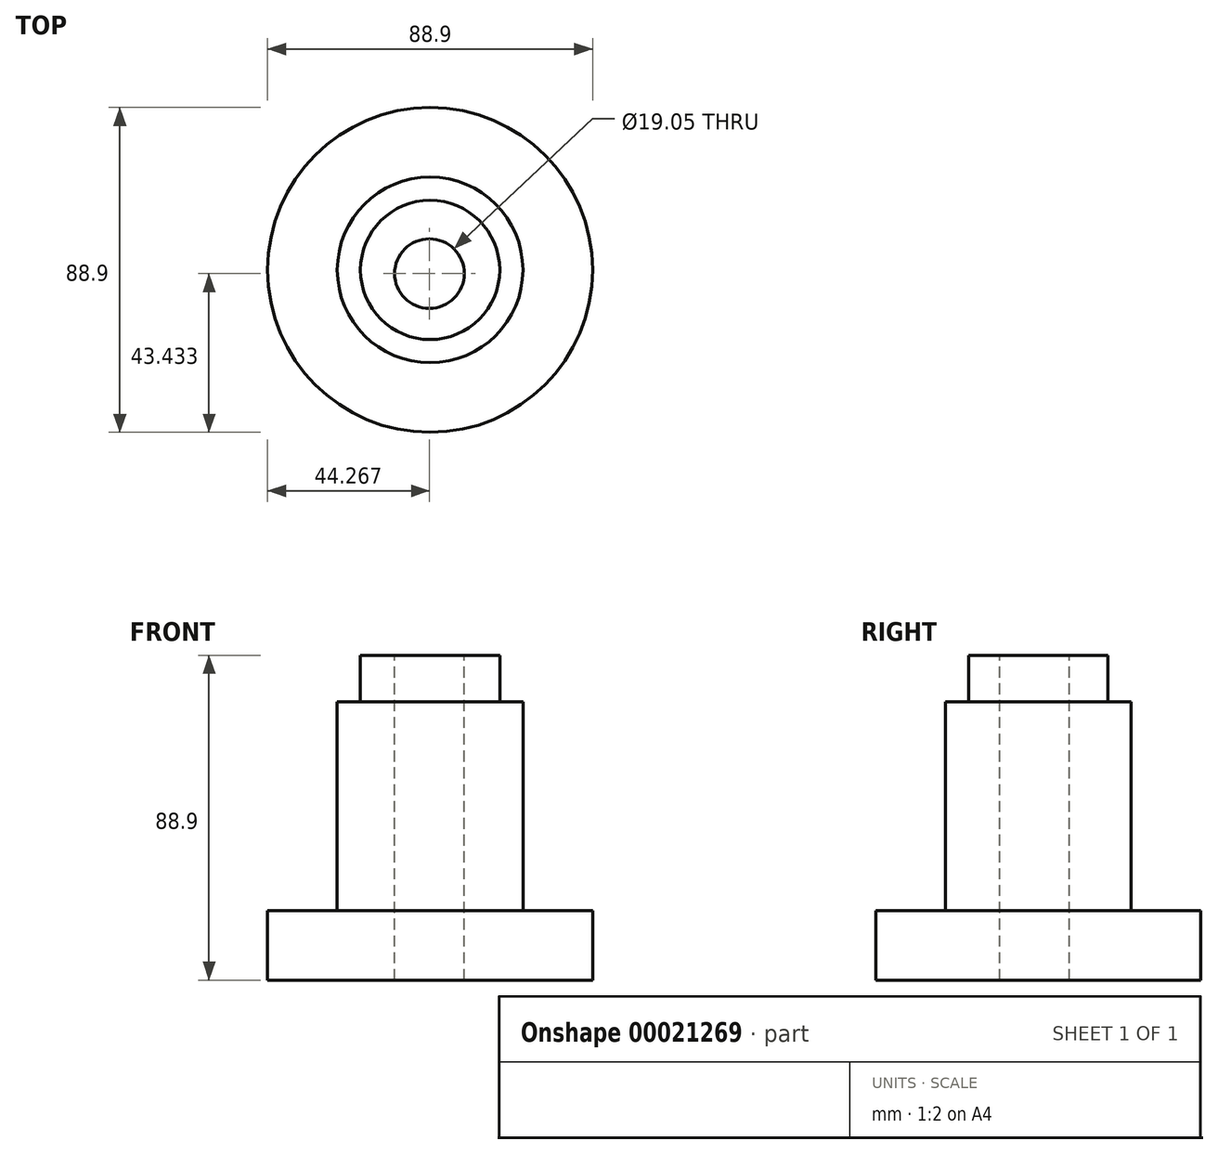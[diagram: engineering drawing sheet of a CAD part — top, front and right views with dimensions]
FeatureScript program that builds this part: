
annotation { "Feature Type Name" : "Feature", "Feature Type Description" : "" }
export const myFeature = defineFeature(function(context is Context, id is Id, definition is map)
    precondition{}
    {
        {
            var Q0;
            Q0=qCreatedBy(makeId("Front.planeOp"),FACE);
            var sketch = newSketch(context, id + "F0", { "sketchPlane" : qUnion([Q0])});
            skLineSegment(sketch, "E0.bottom", {"start": v(-65.1, -12.34) * mm, "end": v(-20.66, -12.34) * mm});
            skLineSegment(sketch, "E0.top", {"start": v(-65.1, -31.39) * mm, "end": v(-20.66, -31.39) * mm});
            skLineSegment(sketch, "E0.left", {"start": v(-65.1, -12.34) * mm, "end": v(-65.1, -31.39) * mm});
            skLineSegment(sketch, "E0.right", {"start": v(-20.66, -12.34) * mm, "end": v(-20.66, -31.39) * mm});
            skLineSegment(sketch, "E1.bottom", {"start": v(-46.06, 44.81) * mm, "end": v(-20.66, 44.81) * mm});
            skLineSegment(sketch, "E1.top", {"start": v(-46.06, -12.34) * mm, "end": v(-20.66, -12.34) * mm});
            skLineSegment(sketch, "E1.left", {"start": v(-46.06, 44.81) * mm, "end": v(-46.06, -12.34) * mm});
            skLineSegment(sketch, "E1.right", {"start": v(-20.66, 44.81) * mm, "end": v(-20.66, -12.34) * mm});
            skLineSegment(sketch, "E2.bottom", {"start": v(-39.7, 57.51) * mm, "end": v(-20.66, 57.51) * mm});
            skLineSegment(sketch, "E2.top", {"start": v(-39.7, 44.81) * mm, "end": v(-20.66, 44.81) * mm});
            skLineSegment(sketch, "E2.left", {"start": v(-39.7, 57.51) * mm, "end": v(-39.7, 44.81) * mm});
            skLineSegment(sketch, "E2.right", {"start": v(-20.66, 57.51) * mm, "end": v(-20.66, 44.81) * mm});
            skSolve(sketch);
        }
        {
            var Q0;
            Q0=makeQuery(id+"F0.imprint","IMPRINT",FACE,{"disambiguationData":[TD([[makeQuery(id+"F0.imprint","IMPRINT",EDGE,{"derivedFrom":sQuery(id+"F0.wireOp",EDGE,"E1.bottom")}),-1.0]])]});
            var Q1;
            Q1=makeQuery(id+"F0.imprint","IMPRINT",FACE,{"disambiguationData":[TD([[makeQuery(id+"F0.imprint","IMPRINT",EDGE,{"derivedFrom":sQuery(id+"F0.wireOp",EDGE,"E2.bottom")}),-1.0]])]});
            var Q2;
            Q2=makeQuery(id+"F0.imprint","IMPRINT",FACE,{"disambiguationData":[TD([[makeQuery(id+"F0.imprint","IMPRINT",EDGE,{"derivedFrom":sQuery(id+"F0.wireOp",EDGE,"E0.bottom")}),-1.0]])]});
            var Q3;
            Q3=sQuery(id+"F0.wireOp",EDGE,"E0.right");
            revolve(context, id + "F1", {"entities" : qUnion([Q0, Q1, Q2]), "axis" : qUnion([Q3]), "revolveType" : RevolveType.FULL});
        }
        {
            var Q0;
            Q0=qCreatedBy(makeId("Top.planeOp"),FACE);
            var sketch = newSketch(context, id + "F2", { "sketchPlane" : qUnion([Q0])});
            skCircle(sketch, "E3", {"center": v(-20.84, -1.02) * mm, "radius": 9.53 * mm});
            skSolve(sketch);
        }
        {
            var Q0;
            Q0 = qSketchRegion(id + "F2", true);
            extrude(context, id + "F3", {"entities" : qUnion([Q0]), "operationType" : NewBodyOperationType.REMOVE, "endBound" : BoundingType.THROUGH_ALL, "oppositeDirection" : true, "depth" : 25.4 * mm});
        }
        {
            var Q0;
            Q0 = qSketchRegion(id + "F2", true);
            extrude(context, id + "F4", {"entities" : qUnion([Q0]), "operationType" : NewBodyOperationType.REMOVE, "endBound" : BoundingType.THROUGH_ALL, "depth" : 25.4 * mm});
        }
    });
